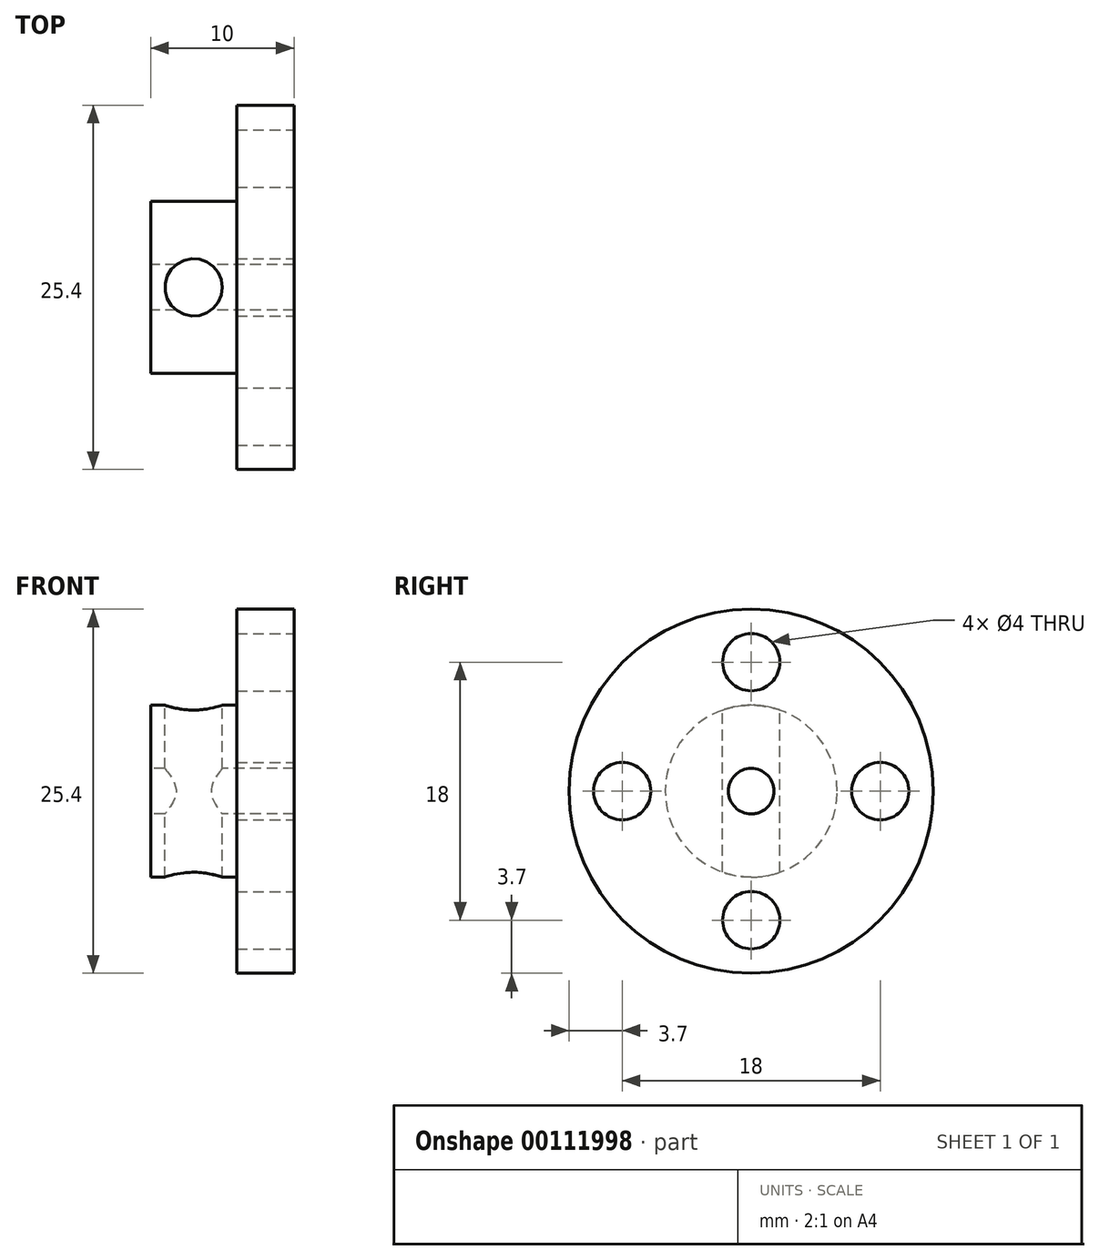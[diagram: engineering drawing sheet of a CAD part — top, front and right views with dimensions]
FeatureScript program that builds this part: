
annotation { "Feature Type Name" : "Feature", "Feature Type Description" : "" }
export const myFeature = defineFeature(function(context is Context, id is Id, definition is map)
    precondition{}
    {
        {
            var Q0;
            Q0=qCreatedBy(makeId("Front.planeOp"),FACE);
            var sketch = newSketch(context, id + "F0", { "sketchPlane" : qUnion([Q0])});
            skLineSegment(sketch, "E0", {"start": v(0, 0) * mm, "end": v(0, 6) * mm});
            skLineSegment(sketch, "E1", {"start": v(0, 6) * mm, "end": v(6, 6) * mm});
            skLineSegment(sketch, "E2", {"start": v(6, 6) * mm, "end": v(6, 12.7) * mm});
            skLineSegment(sketch, "E3", {"start": v(6, 12.7) * mm, "end": v(10, 12.7) * mm});
            skLineSegment(sketch, "E4", {"start": v(10, 12.7) * mm, "end": v(10, 0) * mm});
            skLineSegment(sketch, "E5", {"start": v(10, 0) * mm, "end": v(0, 0) * mm});
            skSolve(sketch);
        }
        {
            var Q0;
            Q0 = qSketchRegion(id + "F0", true);
            var Q1;
            Q1=sQuery(id+"F0.wireOp",EDGE,"E5");
            revolve(context, id + "F1", {"entities" : qUnion([Q0]), "axis" : qUnion([Q1]), "revolveType" : RevolveType.FULL});
        }
        {
            var Q0;
            Q0=qCreatedBy(makeId("Top.planeOp"),FACE);
            var sketch = newSketch(context, id + "F2", { "sketchPlane" : qUnion([Q0])});
            skCircle(sketch, "E6", {"center": v(3, 0) * mm, "radius": 2 * mm});
            skSolve(sketch);
        }
        {
            var Q0;
            Q0 = qSketchRegion(id + "F2", true);
            extrude(context, id + "F3", {"entities" : qUnion([Q0]), "operationType" : NewBodyOperationType.REMOVE, "endBound" : BoundingType.THROUGH_ALL, "oppositeDirection" : true, "depth" : 25 * mm, "hasSecondDirection" : true, "secondDirectionBound" : SecondDirectionBoundingType.THROUGH_ALL, "secondDirectionOppositeDirection" : false, "secondDirectionDepth" : 25 * mm});
        }
        {
            var Q0;
            Q0=makeQuery(id+"F1.opRevolve","SWEPT_FACE",FACE,{"disambiguationData":[OSD([sQuery(id+"F0.wireOp",EDGE,"E4")])]});
            var sketch = newSketch(context, id + "F4", { "sketchPlane" : qUnion([Q0])});
            skCircle(sketch, "E7", {"center": v(0, 0) * mm, "radius": 9 * mm, "construction": true});
            skCircle(sketch, "E8", {"center": v(0, 9) * mm, "radius": 2 * mm});
            skCircle(sketch, "E9", {"center": v(9, 0) * mm, "radius": 2 * mm});
            skCircle(sketch, "E10", {"center": v(0, -9) * mm, "radius": 2 * mm});
            skCircle(sketch, "E11", {"center": v(-9, 0) * mm, "radius": 2 * mm});
            skSolve(sketch);
        }
        {
            var Q0;
            Q0 = qSketchRegion(id + "F4", true);
            extrude(context, id + "F5", {"entities" : qUnion([Q0]), "operationType" : NewBodyOperationType.REMOVE, "endBound" : BoundingType.THROUGH_ALL, "oppositeDirection" : true, "depth" : 25 * mm});
        }
        {
            var Q0;
            Q0=makeQuery(id+"F1.opRevolve","SWEPT_FACE",FACE,{"disambiguationData":[OSD([sQuery(id+"F0.wireOp",EDGE,"E0")])]});
            var sketch = newSketch(context, id + "F6", { "sketchPlane" : qUnion([Q0])});
            skCircle(sketch, "E12", {"center": v(0, 0) * mm, "radius": 1.59 * mm});
            skSolve(sketch);
        }
        {
            var Q0;
            Q0 = qSketchRegion(id + "F6", true);
            extrude(context, id + "F7", {"entities" : qUnion([Q0]), "operationType" : NewBodyOperationType.REMOVE, "endBound" : BoundingType.THROUGH_ALL, "oppositeDirection" : true, "depth" : 25 * mm});
        }
    });
